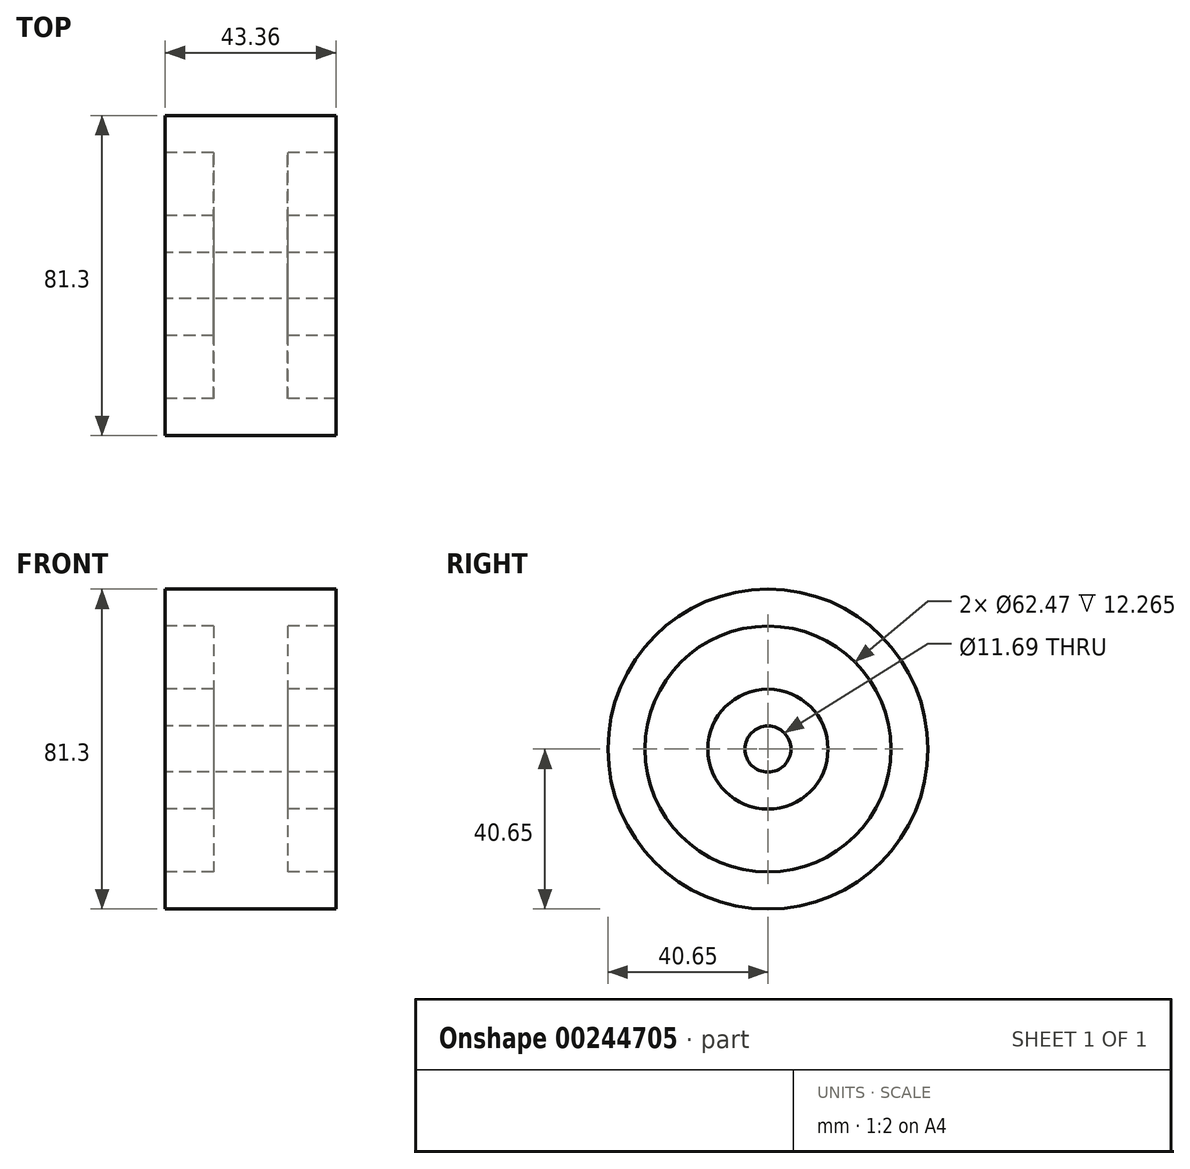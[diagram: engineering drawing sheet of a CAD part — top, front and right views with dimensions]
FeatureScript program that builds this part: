
annotation { "Feature Type Name" : "Feature", "Feature Type Description" : "" }
export const myFeature = defineFeature(function(context is Context, id is Id, definition is map)
    precondition{}
    {
        {
            var Q0;
            Q0=qCreatedBy(makeId("Front.planeOp"),FACE);
            var sketch = newSketch(context, id + "F0", { "sketchPlane" : qUnion([Q0])});
            skLineSegment(sketch, "E0", {"start": v(-30.49, 0) * mm, "end": v(44.94, 0) * mm, "construction": true});
            skLineSegment(sketch, "E1", {"start": v(0, 54.9) * mm, "end": v(0, -28.38) * mm, "construction": true});
            skLineSegment(sketch, "E2", {"start": v(-21.68, 5.85) * mm, "end": v(21.68, 5.85) * mm});
            skLineSegment(sketch, "E3", {"start": v(21.68, 5.85) * mm, "end": v(21.68, 15.26) * mm});
            skLineSegment(sketch, "E4", {"start": v(21.68, 15.26) * mm, "end": v(9.41, 15.26) * mm});
            skLineSegment(sketch, "E5", {"start": v(9.41, 15.26) * mm, "end": v(9.41, 31.23) * mm});
            skLineSegment(sketch, "E6", {"start": v(9.41, 31.23) * mm, "end": v(21.68, 31.23) * mm});
            skLineSegment(sketch, "E7", {"start": v(21.68, 31.23) * mm, "end": v(21.68, 40.65) * mm});
            skLineSegment(sketch, "E8", {"start": v(21.68, 40.65) * mm, "end": v(-21.68, 40.65) * mm});
            skLineSegment(sketch, "E9", {"start": v(-21.68, 40.65) * mm, "end": v(-21.68, 31.23) * mm});
            skLineSegment(sketch, "E10", {"start": v(-21.68, 31.23) * mm, "end": v(-9.41, 31.23) * mm});
            skLineSegment(sketch, "E11", {"start": v(-9.41, 31.23) * mm, "end": v(-9.41, 15.26) * mm});
            skLineSegment(sketch, "E12", {"start": v(-9.41, 15.26) * mm, "end": v(-21.68, 15.26) * mm});
            skLineSegment(sketch, "E13", {"start": v(-21.68, 15.26) * mm, "end": v(-21.68, 5.85) * mm});
            skSolve(sketch);
        }
        {
            var Q0;
            Q0 = qSketchRegion(id + "F0", true);
            var Q1;
            Q1=sQuery(id+"F0.wireOp",EDGE,"E0");
            revolve(context, id + "F1", {"entities" : qUnion([Q0]), "axis" : qUnion([Q1]), "revolveType" : RevolveType.FULL});
        }
    });
